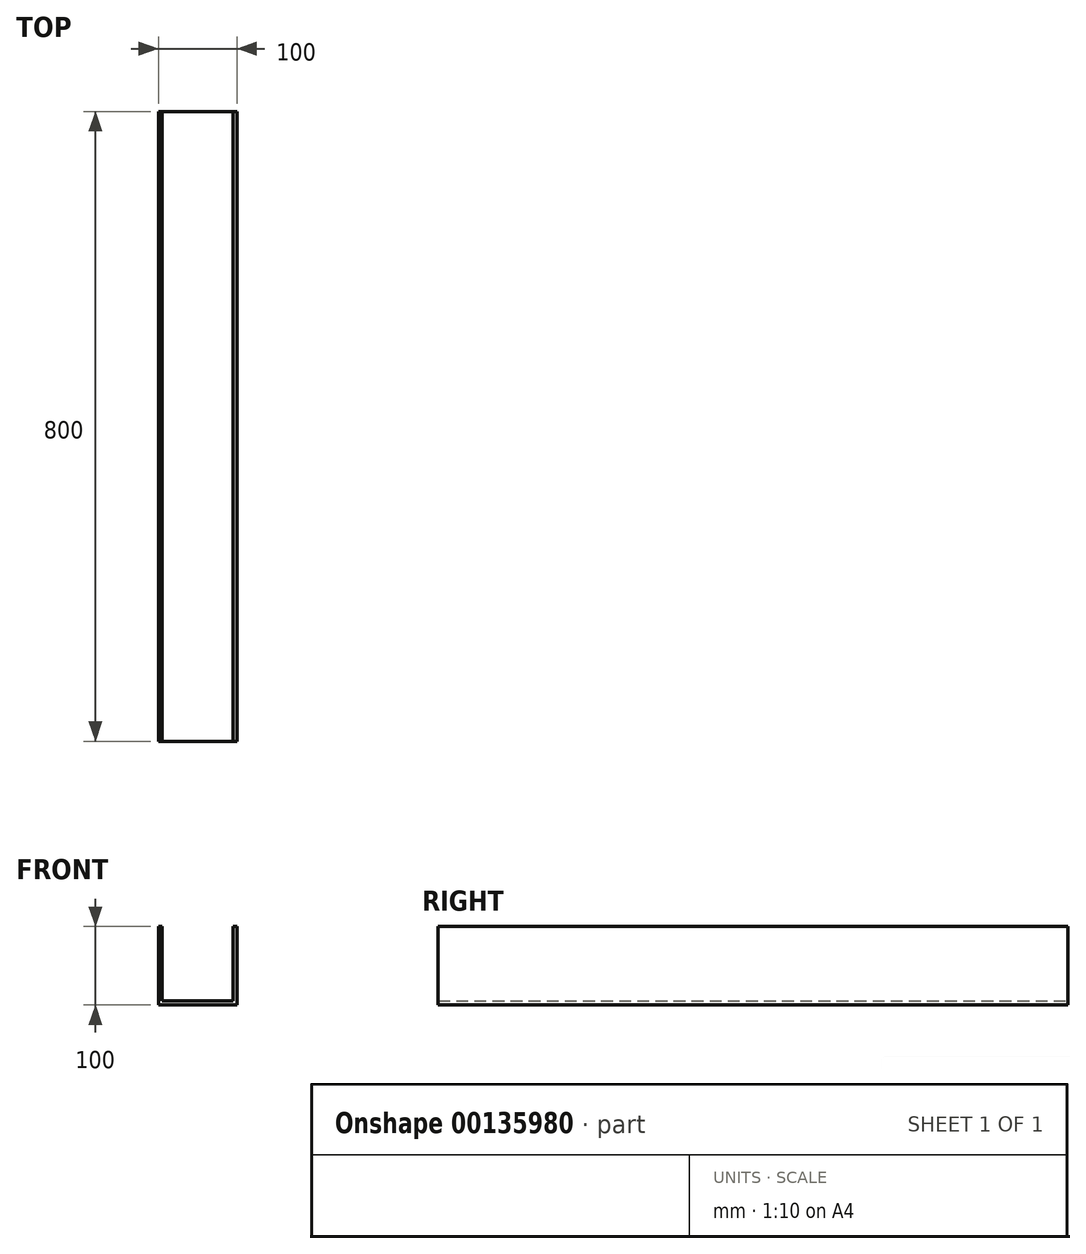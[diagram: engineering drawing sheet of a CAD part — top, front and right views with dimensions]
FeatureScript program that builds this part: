
annotation { "Feature Type Name" : "Feature", "Feature Type Description" : "" }
export const myFeature = defineFeature(function(context is Context, id is Id, definition is map)
    precondition{}
    {
        {
            var Q0;
            Q0=qCreatedBy(makeId("Front.planeOp"),FACE);
            var sketch = newSketch(context, id + "F0", { "sketchPlane" : qUnion([Q0])});
            skLineSegment(sketch, "E0", {"start": v(-50, 50) * mm, "end": v(-50, -50) * mm});
            skLineSegment(sketch, "E1", {"start": v(-50, -50) * mm, "end": v(50, -50) * mm});
            skLineSegment(sketch, "E2", {"start": v(50, -50) * mm, "end": v(50, 50) * mm});
            skLineSegment(sketch, "E3", {"start": v(50, 50) * mm, "end": v(45, 50) * mm});
            skLineSegment(sketch, "E4", {"start": v(45, 50) * mm, "end": v(45, -45) * mm});
            skLineSegment(sketch, "E5", {"start": v(45, -45) * mm, "end": v(-45, -45) * mm});
            skLineSegment(sketch, "E6", {"start": v(-45, -45) * mm, "end": v(-45, 50) * mm});
            skLineSegment(sketch, "E7", {"start": v(-45, 50) * mm, "end": v(-50, 50) * mm});
            skSolve(sketch);
        }
        {
            var Q0;
            Q0=makeQuery(id+"F0.imprint","IMPRINT",FACE,{"disambiguationData":[TD([[makeQuery(id+"F0.imprint","IMPRINT",EDGE,{"derivedFrom":sQuery(id+"F0.wireOp",EDGE,"E0")}),1.0]])]});
            extrude(context, id + "F1", {"entities" : qUnion([Q0]), "endBound" : BoundingType.SYMMETRIC, "depth" : 800 * mm});
        }
    });
